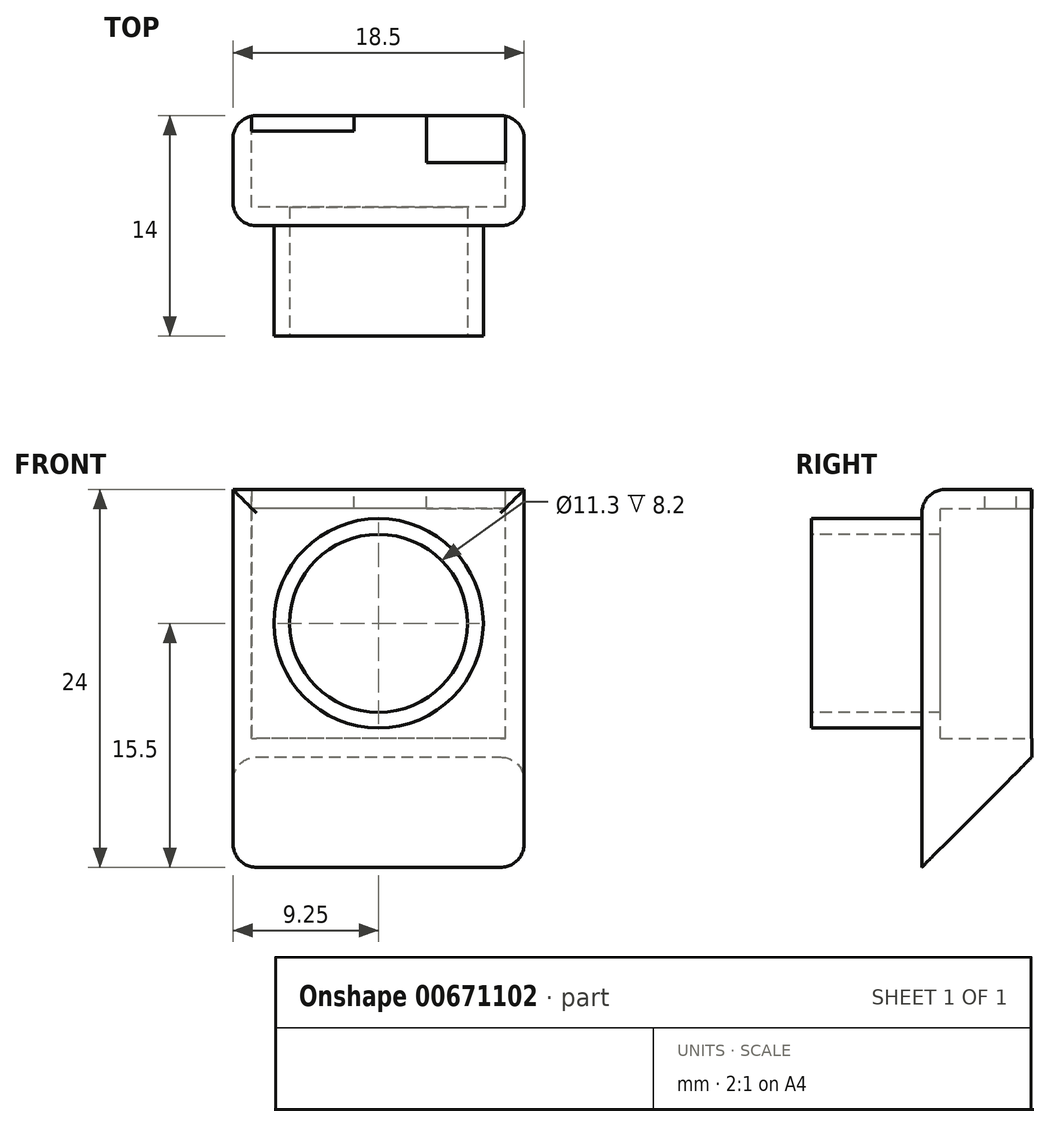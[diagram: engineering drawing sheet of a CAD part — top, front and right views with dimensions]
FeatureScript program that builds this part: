
annotation { "Feature Type Name" : "Feature", "Feature Type Description" : "" }
export const myFeature = defineFeature(function(context is Context, id is Id, definition is map)
    precondition{}
    {
        {
            var Q0;
            Q0=qCreatedBy(makeId("Front.planeOp"),FACE);
            var sketch = newSketch(context, id + "F0", { "sketchPlane" : qUnion([Q0])});
            skLineSegment(sketch, "E0.bottom", {"start": v(9.25, -8.5) * mm, "end": v(-9.25, -8.5) * mm});
            skLineSegment(sketch, "E0.top", {"start": v(9.25, 8.5) * mm, "end": v(-9.25, 8.5) * mm});
            skLineSegment(sketch, "E0.left", {"start": v(9.25, -8.5) * mm, "end": v(9.25, 8.5) * mm});
            skLineSegment(sketch, "E0.right", {"start": v(-9.25, -8.5) * mm, "end": v(-9.25, 8.5) * mm});
            skPoint(sketch, "E0.middle", {"position": v(0, 0) * mm});
            skSolve(sketch);
        }
        {
            var Q0;
            Q0 = qSketchRegion(id + "F0", true);
            extrude(context, id + "F1", {"entities" : qUnion([Q0]), "depth" : 7 * mm, "offsetDistance" : 25 * mm});
        }
        {
            var Q0;
            Q0=makeQuery(id+"F1.opExtrude","CAP_FACE",FACE,{"disambiguationData":[OSD([sQuery(id+"F0.wireOp",EDGE,"E0.bottom"),sQuery(id+"F0.wireOp",EDGE,"E0.top"),sQuery(id+"F0.wireOp",EDGE,"E0.left"),sQuery(id+"F0.wireOp",EDGE,"E0.right")])],"isStart":true});
            shell(context, id + "F2", {"entities" : qUnion([Q0]), "thickness" : 1.2 * mm});
        }
        {
            var Q0;
            Q0=makeQuery(id+"F1.opExtrude","CAP_FACE",FACE,{"disambiguationData":[OSD([sQuery(id+"F0.wireOp",EDGE,"E0.bottom"),sQuery(id+"F0.wireOp",EDGE,"E0.top"),sQuery(id+"F0.wireOp",EDGE,"E0.left"),sQuery(id+"F0.wireOp",EDGE,"E0.right")])],"isStart":false});
            var sketch = newSketch(context, id + "F3", { "sketchPlane" : qUnion([Q0])});
            skCircle(sketch, "E1", {"center": v(0, 0) * mm, "radius": 5.65 * mm});
            skCircle(sketch, "E2.0", {"center": v(0, 0) * mm, "radius": 6.65 * mm});
            skSolve(sketch);
        }
        {
            var Q0;
            Q0=makeQuery(id+"F3.imprint","IMPRINT",FACE,{"disambiguationData":[TD([[makeQuery(id+"F3.imprint","IMPRINT",EDGE,{"derivedFrom":sQuery(id+"F3.wireOp",EDGE,"E1")}),1.0]])]});
            extrude(context, id + "F4", {"entities" : qUnion([Q0]), "operationType" : NewBodyOperationType.REMOVE, "oppositeDirection" : true, "depth" : 4 * mm, "offsetDistance" : 25 * mm});
        }
        {
            var Q0;
            Q0 = qSketchRegion(id + "F3", true);
            extrude(context, id + "F5", {"entities" : qUnion([Q0]), "operationType" : NewBodyOperationType.ADD, "depth" : 7 * mm, "offsetDistance" : 25 * mm});
        }
        {
            var Q0;
            Q0=makeQuery(id+"F1.opExtrude","SWEPT_FACE",FACE,{"disambiguationData":[OSD([sQuery(id+"F0.wireOp",EDGE,"E0.top")])]});
            var sketch = newSketch(context, id + "F6", { "sketchPlane" : qUnion([Q0])});
            skLineSegment(sketch, "E3.bottom", {"start": v(-8.05, 0) * mm, "end": v(-1.55, 0) * mm});
            skLineSegment(sketch, "E3.top", {"start": v(-8.05, -1) * mm, "end": v(-1.55, -1) * mm});
            skLineSegment(sketch, "E3.left", {"start": v(-8.05, 0) * mm, "end": v(-8.05, -1) * mm});
            skLineSegment(sketch, "E3.right", {"start": v(-1.55, 0) * mm, "end": v(-1.55, -1) * mm});
            skLineSegment(sketch, "E4.bottom", {"start": v(8.05, 0) * mm, "end": v(3.05, 0) * mm});
            skLineSegment(sketch, "E4.top", {"start": v(8.05, -3) * mm, "end": v(3.05, -3) * mm});
            skLineSegment(sketch, "E4.left", {"start": v(8.05, 0) * mm, "end": v(8.05, -3) * mm});
            skLineSegment(sketch, "E4.right", {"start": v(3.05, 0) * mm, "end": v(3.05, -3) * mm});
            skSolve(sketch);
        }
        {
            var Q0;
            Q0 = qSketchRegion(id + "F6", true);
            extrude(context, id + "F7", {"entities" : qUnion([Q0]), "operationType" : NewBodyOperationType.REMOVE, "oppositeDirection" : true, "depth" : 3 * mm, "offsetDistance" : 25 * mm});
        }
        {
            var Q0;
            Q0=makeQuery(id+"F1.opExtrude","SWEPT_FACE",FACE,{"disambiguationData":[OSD([sQuery(id+"F0.wireOp",EDGE,"E0.bottom")])]});
            extrude(context, id + "F8", {"entities" : qUnion([Q0]), "operationType" : NewBodyOperationType.ADD, "depth" : 7 * mm, "offsetDistance" : 25 * mm});
        }
        {
            var Q0;
            {var subQ0=sQuery(id+"F0.wireOp",EDGE,"E0.left");Q0=makeQuery(id+"F8.boolean.opBoolean","MERGE",FACE,{"derivedFrom":[makeQuery(id+"F1.opExtrude","SWEPT_FACE",FACE,{"disambiguationData":[OSD([subQ0])]}),makeQuery(id+"F8.opExtrude","SWEPT_FACE",FACE,{"disambiguationData":[OSD([sQuery(id+"F0.wireOp",EDGE,"E0.bottom"),subQ0])]})]});}
            var sketch = newSketch(context, id + "F9", { "sketchPlane" : qUnion([Q0])});
            skLineSegment(sketch, "E5", {"start": v(-7, -15.5) * mm, "end": v(0, -8.5) * mm});
            skSolve(sketch);
        }
        {
            var Q0;
            {var subQ0=sQuery(id+"F9.wireOp",EDGE,"E5");Q0=makeQuery(id+"F9.imprint","IMPRINT",FACE,{"disambiguationData":[TD([[makeQuery(id+"F9.imprint","IMPRINT",EDGE,{"derivedFrom":subQ0}),-1.0]])]});}
            extrude(context, id + "F10", {"entities" : qUnion([Q0]), "operationType" : NewBodyOperationType.REMOVE, "oppositeDirection" : true, "depth" : 25 * mm, "offsetDistance" : 25 * mm});
        }
        {
            var Q0;
            {var subQ0=sQuery(id+"F0.wireOp",EDGE,"E0.left");var subQ1=sQuery(id+"F0.wireOp",EDGE,"E0.bottom");Q0=makeQuery(id+"F8.boolean.opBoolean","MERGE",EDGE,{"derivedFrom":[makeQuery(id+"F1.opExtrude","CAP_EDGE",EDGE,{"disambiguationData":[OSD([subQ0])],"isStart":false}),makeQuery(id+"F8.opExtrude","SWEPT_EDGE",EDGE,{"disambiguationData":[OSD([subQ1,subQ0]),TDD([makeQuery(id+"F1.opExtrude","CAP_VERTEX",VERTEX,{"disambiguationData":[OSD([subQ1,subQ0])],"isStart":false})])]})]});}
            var Q1;
            {var subQ0=sQuery(id+"F0.wireOp",EDGE,"E0.left");var subQ1=sQuery(id+"F0.wireOp",EDGE,"E0.bottom");Q1=makeQuery(id+"F8.boolean.opBoolean","MERGE",EDGE,{"derivedFrom":[makeQuery(id+"F1.opExtrude","CAP_EDGE",EDGE,{"disambiguationData":[OSD([subQ0])],"isStart":true}),makeQuery(id+"F8.opExtrude","SWEPT_EDGE",EDGE,{"disambiguationData":[OSD([subQ1,subQ0]),TDD([makeQuery(id+"F1.opExtrude","CAP_VERTEX",VERTEX,{"disambiguationData":[OSD([subQ1,subQ0])],"isStart":true})])]})]});}
            var Q2;
            {var subQ0=sQuery(id+"F0.wireOp",EDGE,"E0.right");var subQ1=sQuery(id+"F0.wireOp",EDGE,"E0.bottom");Q2=makeQuery(id+"F8.boolean.opBoolean","MERGE",EDGE,{"derivedFrom":[makeQuery(id+"F1.opExtrude","CAP_EDGE",EDGE,{"disambiguationData":[OSD([subQ0])],"isStart":false}),makeQuery(id+"F8.opExtrude","SWEPT_EDGE",EDGE,{"disambiguationData":[OSD([subQ1,subQ0]),TDD([makeQuery(id+"F1.opExtrude","CAP_VERTEX",VERTEX,{"disambiguationData":[OSD([subQ1,subQ0])],"isStart":false})])]})]});}
            var Q3;
            {var subQ0=sQuery(id+"F0.wireOp",EDGE,"E0.right");var subQ1=sQuery(id+"F0.wireOp",EDGE,"E0.bottom");Q3=makeQuery(id+"F8.boolean.opBoolean","MERGE",EDGE,{"derivedFrom":[makeQuery(id+"F1.opExtrude","CAP_EDGE",EDGE,{"disambiguationData":[OSD([subQ0])],"isStart":true}),makeQuery(id+"F8.opExtrude","SWEPT_EDGE",EDGE,{"disambiguationData":[OSD([subQ1,subQ0]),TDD([makeQuery(id+"F1.opExtrude","CAP_VERTEX",VERTEX,{"disambiguationData":[OSD([subQ1,subQ0])],"isStart":true})])]})]});}
            var Q4;
            Q4=makeQuery(id+"F1.opExtrude","CAP_EDGE",EDGE,{"disambiguationData":[OSD([sQuery(id+"F0.wireOp",EDGE,"E0.top")])],"isStart":false});
            fillet(context, id + "F11", {"entities" : qUnion([Q0, Q1, Q2, Q3, Q4]), "radius" : 1.5 * mm, "tangentPropagation" : true, "allowEdgeOverflow" : false});
        }
    });
